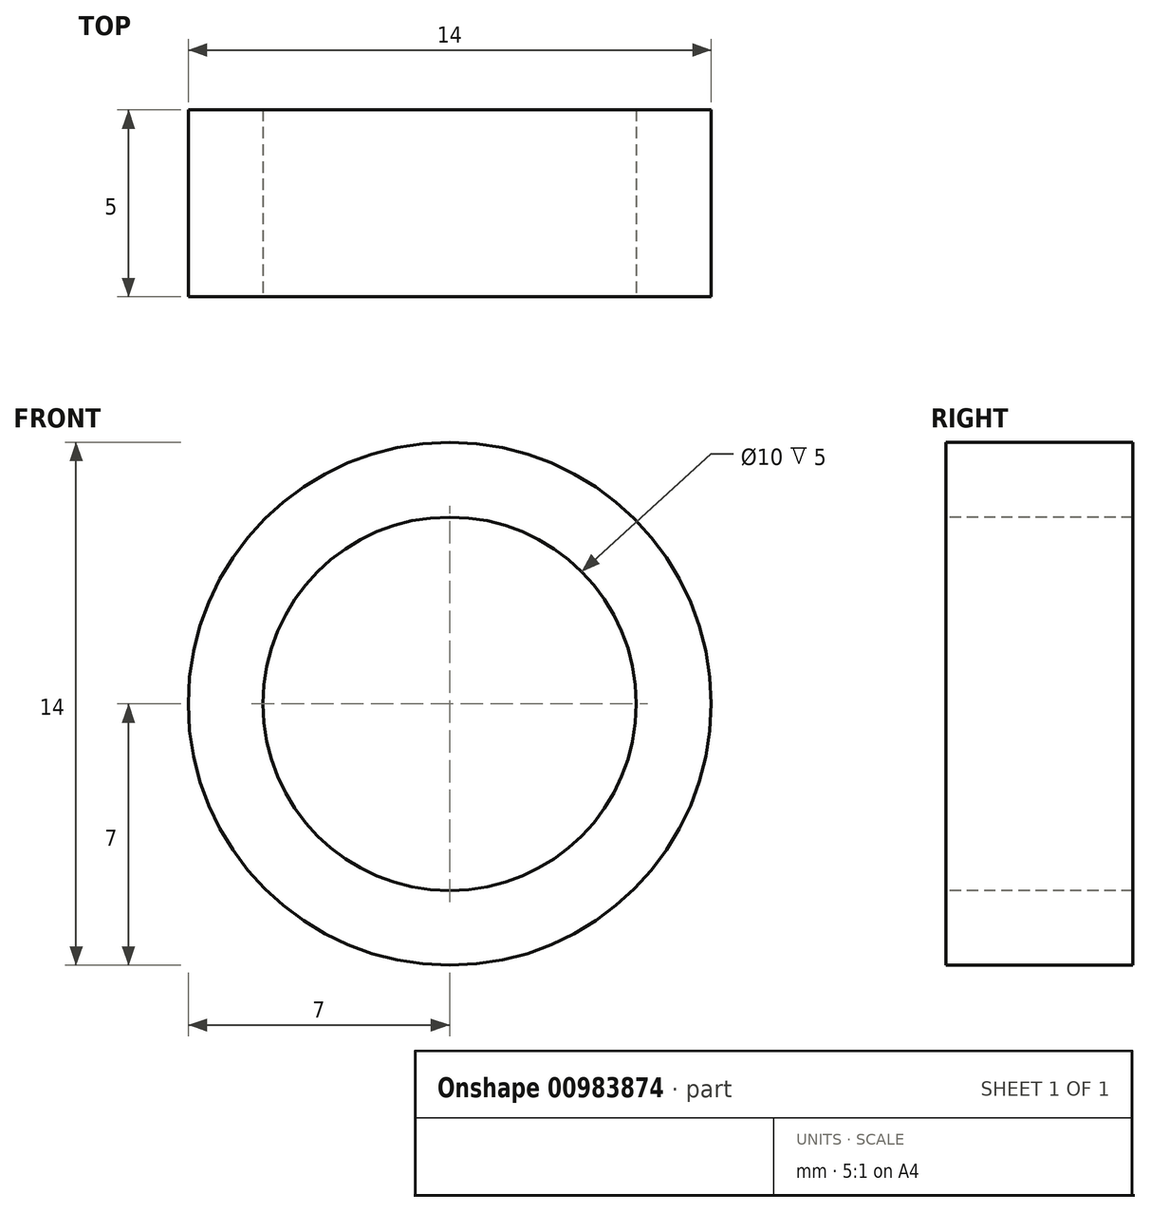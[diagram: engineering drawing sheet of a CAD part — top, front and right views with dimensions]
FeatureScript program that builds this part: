
annotation { "Feature Type Name" : "Feature", "Feature Type Description" : "" }
export const myFeature = defineFeature(function(context is Context, id is Id, definition is map)
    precondition{}
    {
        {
            var Q0;
            Q0=qCreatedBy(makeId("Front.planeOp"),FACE);
            var sketch = newSketch(context, id + "F0", { "sketchPlane" : qUnion([Q0])});
            skCircle(sketch, "E0", {"center": v(0, 0) * mm, "radius": 5 * mm});
            skCircle(sketch, "E1", {"center": v(0, 0) * mm, "radius": 7 * mm});
            skSolve(sketch);
        }
        {
            var Q0;
            Q0=makeQuery(id+"F0.imprint","IMPRINT",FACE,{"disambiguationData":[TD([[makeQuery(id+"F0.imprint","IMPRINT",EDGE,{"derivedFrom":sQuery(id+"F0.wireOp",EDGE,"E0")}),-1.0]])]});
            extrude(context, id + "F1", {"entities" : qUnion([Q0]), "oppositeDirection" : true, "depth" : 5 * mm, "offsetDistance" : 25 * mm});
        }
    });
